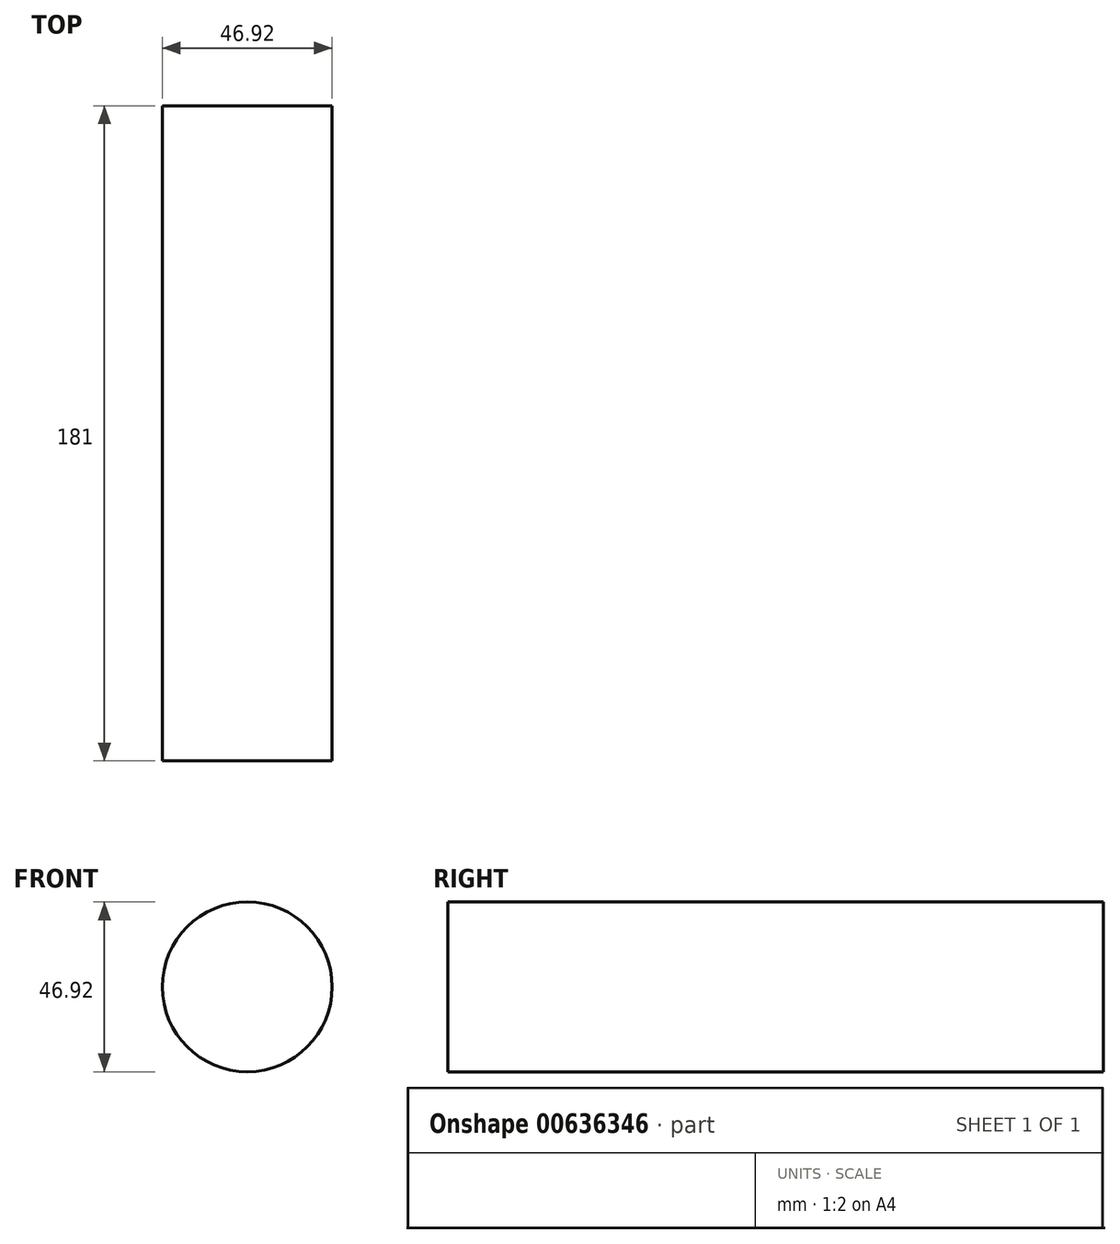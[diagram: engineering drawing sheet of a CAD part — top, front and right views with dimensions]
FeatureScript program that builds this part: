
annotation { "Feature Type Name" : "Feature", "Feature Type Description" : "" }
export const myFeature = defineFeature(function(context is Context, id is Id, definition is map)
    precondition{}
    {
        {
            var Q0;
            Q0=qCreatedBy(makeId("Front.planeOp"),FACE);
            var sketch = newSketch(context, id + "F0", { "sketchPlane" : qUnion([Q0])});
            skCircle(sketch, "E0", {"center": v(0, 0) * mm, "radius": 23.46 * mm});
            skSolve(sketch);
        }
        {
            var Q0;
            Q0 = qSketchRegion(id + "F0", true);
            extrude(context, id + "F1", {"entities" : qUnion([Q0]), "depth" : 181 * mm, "offsetDistance" : 25 * mm});
        }
    });
